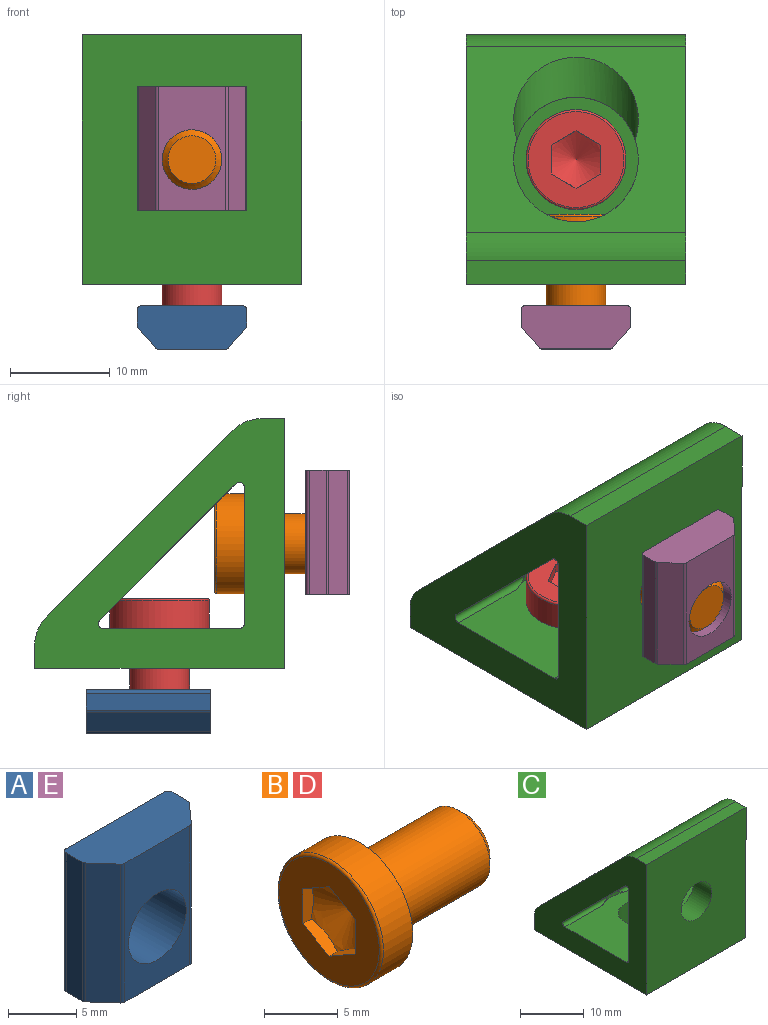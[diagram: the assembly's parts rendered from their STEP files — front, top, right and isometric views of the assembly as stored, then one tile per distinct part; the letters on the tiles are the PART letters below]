
ASSEMBLY  parts=5 mates=4
PART A: 15 faces, bbox 10.9x4.3x12.4 mm
  f0: cylinder r=0.38mm len=12.45mm, axis (0,0,-1), area 3.5mm2, adj f1,f11,f12,f13
  f1: plane 12.45x1.65mm, normal (1,0,0), area 20.5mm2, adj f0,f2,f12,f13
  f2: cylinder r=0.38mm len=12.45mm, axis (0,0,-1), area 7.4mm2, adj f1,f3,f12,f13
  f3: plane 12.45x10.19mm, normal (0,1,0), area 98.7mm2, adj f2,f4,f12,f13,f14
  f4: cylinder r=0.38mm len=12.45mm, axis (0,0,-1), area 7.4mm2, adj f3,f5,f12,f13
  f5: plane 12.45x1.65mm, normal (-1,0,0), area 20.5mm2, adj f4,f6,f12,f13
  f6: cylinder r=0.38mm len=12.45mm, axis (0,0,-1), area 3.5mm2, adj f5,f7,f12,f13
  f7: plane 12.45x1.94mm, normal (-0.75,-0.67,0), area 32.3mm2, adj f6,f8,f12,f13
  f8: cylinder r=0.38mm len=12.45mm, axis (0,0,-1), area 4mm2, adj f7,f9,f12,f13
  f9: plane 12.45x6.72mm, normal (0,-1,0), area 55.6mm2, adj f8,f10,f12,f13,f14
  f10: cylinder r=0.38mm len=12.45mm, axis (0,0,-1), area 4mm2, adj f9,f11,f12,f13
  f11: plane 12.45x1.94mm, normal (0.75,-0.67,0), area 32.3mm2, adj f0,f10,f12,f13
  f12: plane 10.95x4.34mm, normal (0,0,1), area 43.3mm2, adj f0,f1,f2,f3,f4,f5,f6,f7
  f13: plane 10.95x4.34mm, normal (0,0,-1), area 43.3mm2, adj f0,f1,f2,f3,f4,f5,f6,f7
  f14: cylinder r=2.99mm len=5.97mm, axis (0,1,0), area 81.5mm2, adj f3,f9
PART B: 14 faces, bbox 13x10.8x10.8 mm
  f0: plane 4.77x4.77mm, normal (1,0,0), area 17.9mm2, adj f2
  f1: cone r=2.9mm half-angle=60deg, axis (-1,0,0), area 25mm2, adj f3,f4,f5,f6,f7,f8
  f2: cone r=2.39mm half-angle=45deg, axis (-1,0,0), area 14.7mm2, adj f0,f9
  f3: plane 2.89x1.01mm, normal (0,-1,0), area 2.7mm2, adj f1,f4,f8,f10
  f4: plane 2.5x1.44mm, normal (0,-0.5,-0.87), area 2.7mm2, adj f1,f3,f5,f10
  f5: plane 2.5x1.44mm, normal (0,0.5,-0.87), area 2.7mm2, adj f1,f4,f6,f10
  f6: plane 2.89x1.01mm, normal (0,1,0), area 2.7mm2, adj f1,f5,f7,f10
  f7: plane 2.5x1.44mm, normal (0,0.5,0.87), area 2.7mm2, adj f1,f6,f8,f10
  f8: plane 2.5x1.44mm, normal (0,-0.5,0.87), area 2.7mm2, adj f1,f3,f7,f10
  f9: cylinder r=3mm len=9.39mm, axis (-1,0,0), area 176.9mm2, adj f2,f11
  f10: plane 9.6x9.6mm, normal (-1,0,0), area 50.7mm2, adj f3,f4,f5,f6,f7,f8,f12
  f11: plane 10x10mm, normal (1,0,0), area 50.3mm2, adj f9,f13
  f12: torus R=4.8mm, axis (-1,0,0), area 9.7mm2, adj f10,f13
  f13: cylinder r=5mm len=10mm, axis (-1,0,0), area 88mm2, adj f11,f12
PART C: 24 faces, bbox 22x25x25 mm
  f0: plane 13.64x13.64mm, normal (0,-0.71,-0.71), area 111.6mm2, adj f1,f3,f4,f20,f23
  f1: cylinder r=0.5mm len=9.77mm, axis (-1,0,0), area 10.9mm2, adj f0,f4,f18,f23
  f2: cylinder r=6.25mm len=12.5mm, axis (0,0,1), area 86.5mm2, adj f8,f22,f23
  f3: cylinder r=0.5mm len=9.78mm, axis (-1,0,0), area 10.7mm2, adj f0,f4,f14,f20
  f4: plane 25x25mm, normal (1,0,0), area 286.7mm2, adj f0,f1,f3,f6,f7,f8,f9,f10
  f5: plane 25x25mm, normal (-1,0,0), area 286.7mm2, adj f6,f7,f8,f9,f10,f11,f12,f13
  f6: plane 22x2.33mm, normal (0,1,0), area 51.2mm2, adj f4,f5,f7,f12
  f7: cylinder r=4mm len=22mm, axis (-1,0,0), area 69mm2, adj f4,f5,f6,f8
  f8: plane 22x18.67mm, normal (0,0.71,0.71), area 338.1mm2, adj f2,f4,f5,f7,f9,f22
  f9: cylinder r=4mm len=22mm, axis (-1,0,0), area 69.1mm2, adj f4,f5,f8,f10
  f10: plane 22x2.33mm, normal (0,0,1), area 51.3mm2, adj f4,f5,f9,f11
  f11: plane 25x22mm, normal (0,-1,0), area 513.7mm2, adj f4,f5,f10,f12,f21
  f12: plane 25x22mm, normal (0,0,-1), area 513.7mm2, adj f4,f5,f6,f11,f19
  f13: cylinder r=0.5mm len=22mm, axis (-1,0,0), area 17.2mm2, adj f4,f5,f14,f18
  f14: plane 22x14.24mm, normal (0,0,1), area 265.9mm2, adj f3,f4,f5,f13,f15,f19,f20
  f15: cylinder r=0.5mm len=9.78mm, axis (-1,0,0), area 10.7mm2, adj f5,f14,f16,f20
  f16: plane 13.64x13.64mm, normal (0,-0.71,-0.71), area 111.6mm2, adj f5,f15,f17,f20,f23
  f17: cylinder r=0.5mm len=9.77mm, axis (-1,0,0), area 10.9mm2, adj f5,f16,f18,f23
  f18: plane 22x14.26mm, normal (0,1,0), area 265.9mm2, adj f1,f4,f5,f13,f17,f21,f23
  f19: cylinder r=3.4mm len=6.8mm, axis (0,0,1), area 85.5mm2, adj f12,f14
  f20: cylinder r=6.25mm len=12.5mm, axis (0,0,1), area 36mm2, adj f0,f3,f14,f15,f16,f22,f23
  f21: cylinder r=3.4mm len=6.8mm, axis (0,1,0), area 85.5mm2, adj f11,f18
  f22: cylinder r=6.25mm len=12.5mm, axis (0,1,0), area 86.5mm2, adj f2,f8,f20
  f23: cylinder r=6.25mm len=12.5mm, axis (0,1,0), area 36.1mm2, adj f0,f1,f2,f16,f17,f18,f20
PART D: same geometry as B
PART E: same geometry as A
PLACE A rot(axis=(0,0.71,0.71),180deg) t=(0,12.5,-14.64)mm
PLACE B rot(axis=(0.58,-0.58,-0.58),120deg) t=(0,4,0)mm
PLACE C at identity fixed
PLACE D rot(axis=(-0.58,0.58,0.58),120deg) t=(0,12.5,-8.5)mm
PLACE E t=(0,-2.14,0)mm
MATE fastened A.f14 <-> C.f2  axis (0,0,1) through (0,12.5,-12.5)mm
MATE fastened B.f1 <-> C.f22  axis (0,1,0) through (0,4,0)mm
MATE fastened E.f14 <-> C.f22  axis (0,1,0) through (0,0,0)mm
MATE fastened D.f1 <-> C.f2  axis (0,0,-1) through (0,12.5,-8.5)mm
